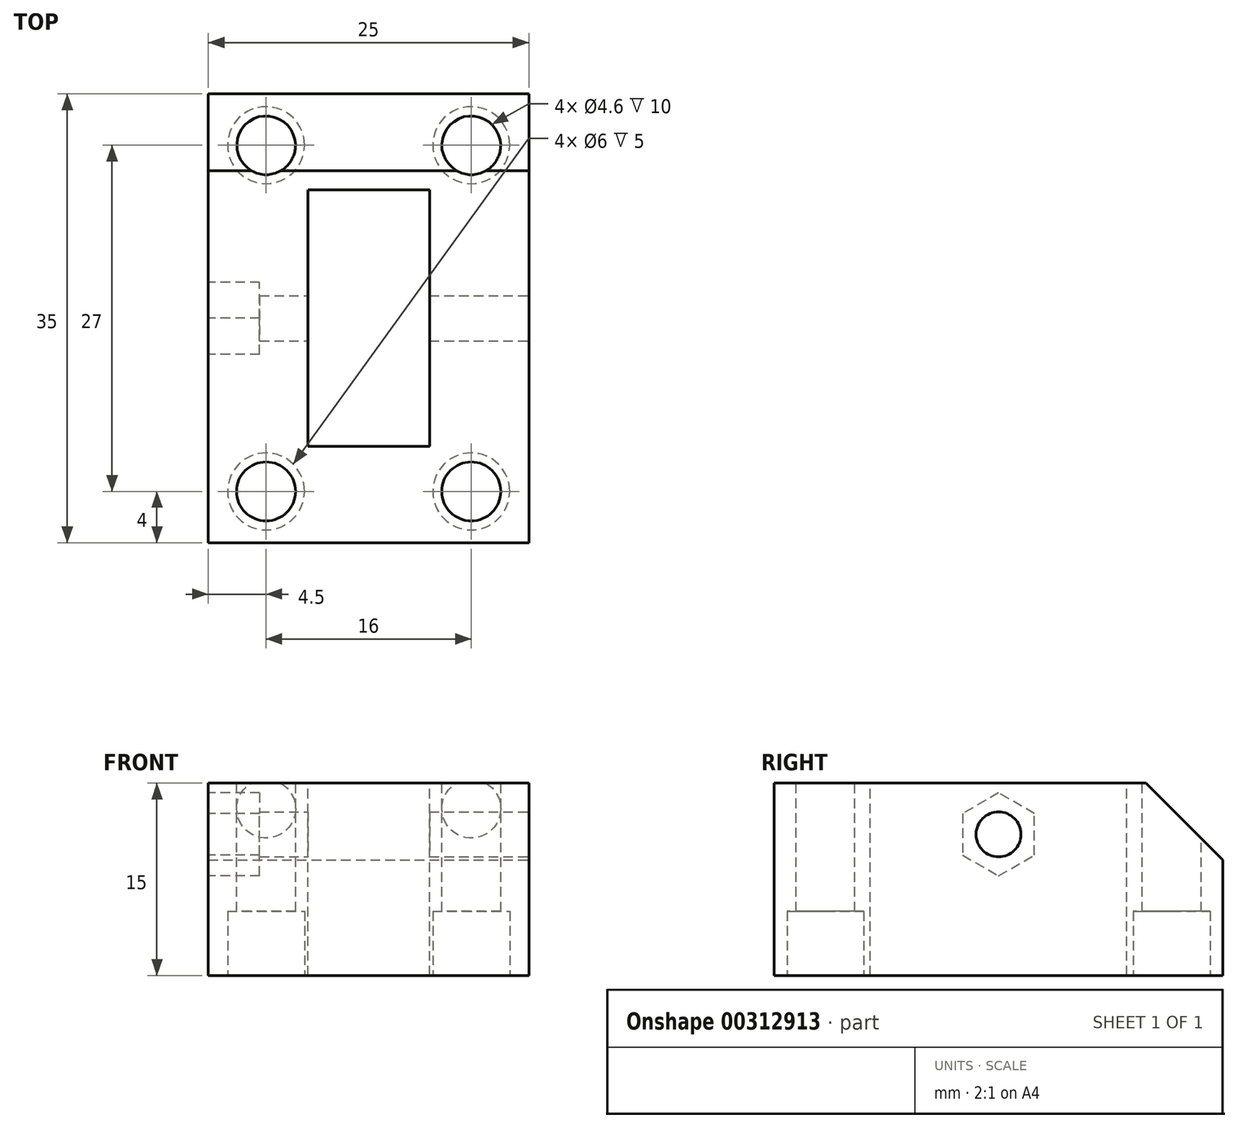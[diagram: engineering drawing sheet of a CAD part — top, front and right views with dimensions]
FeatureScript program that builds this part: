
annotation { "Feature Type Name" : "Feature", "Feature Type Description" : "" }
export const myFeature = defineFeature(function(context is Context, id is Id, definition is map)
    precondition{}
    {
        {
            var Q0;
            Q0=qCreatedBy(makeId("Top.planeOp"),FACE);
            var sketch = newSketch(context, id + "F0", { "sketchPlane" : qUnion([Q0])});
            skLineSegment(sketch, "E0.bottom", {"start": v(-12.5, 17.5) * mm, "end": v(12.5, 17.5) * mm});
            skLineSegment(sketch, "E0.top", {"start": v(-12.5, -17.5) * mm, "end": v(12.5, -17.5) * mm});
            skLineSegment(sketch, "E0.left", {"start": v(-12.5, 17.5) * mm, "end": v(-12.5, -17.5) * mm});
            skLineSegment(sketch, "E0.right", {"start": v(12.5, 17.5) * mm, "end": v(12.5, -17.5) * mm});
            skSolve(sketch);
        }
        {
            var Q0;
            Q0=makeQuery(id+"F0.imprint","IMPRINT",FACE,{"disambiguationData":[TD([[makeQuery(id+"F0.imprint","IMPRINT",EDGE,{"derivedFrom":sQuery(id+"F0.wireOp",EDGE,"E0.bottom")}),-1.0]])]});
            extrude(context, id + "F1", {"entities" : qUnion([Q0]), "oppositeDirection" : true, "depth" : 15 * mm});
        }
        {
            var Q0;
            Q0=makeQuery(id+"F1.opExtrude","SWEPT_FACE",FACE,{"disambiguationData":[OSD([sQuery(id+"F0.wireOp",EDGE,"E0.right")])]});
            var sketch = newSketch(context, id + "F2", { "sketchPlane" : qUnion([Q0])});
            skCircle(sketch, "E1", {"center": v(0, -4) * mm, "radius": 1.75 * mm});
            skSolve(sketch);
        }
        {
            var Q0;
            Q0=makeQuery(id+"F2.imprint","IMPRINT",FACE,{"disambiguationData":[TD([[makeQuery(id+"F2.imprint","IMPRINT",EDGE,{"derivedFrom":sQuery(id+"F2.wireOp",EDGE,"E1")}),1.0]])]});
            extrude(context, id + "F3", {"entities" : qUnion([Q0]), "operationType" : NewBodyOperationType.REMOVE, "oppositeDirection" : true, "depth" : 25 * mm});
        }
        {
            var Q0;
            Q0=makeQuery(id+"F1.opExtrude","CAP_FACE",FACE,{"disambiguationData":[OSD([sQuery(id+"F0.wireOp",EDGE,"E0.bottom"),sQuery(id+"F0.wireOp",EDGE,"E0.top"),sQuery(id+"F0.wireOp",EDGE,"E0.left"),sQuery(id+"F0.wireOp",EDGE,"E0.right")])],"isStart":true});
            var sketch = newSketch(context, id + "F4", { "sketchPlane" : qUnion([Q0])});
            skLineSegment(sketch, "E2.bottom", {"start": v(-4.75, 10) * mm, "end": v(4.75, 10) * mm});
            skLineSegment(sketch, "E2.top", {"start": v(-4.75, -10) * mm, "end": v(4.75, -10) * mm});
            skLineSegment(sketch, "E2.left", {"start": v(-4.75, 10) * mm, "end": v(-4.75, -10) * mm});
            skLineSegment(sketch, "E2.right", {"start": v(4.75, 10) * mm, "end": v(4.75, -10) * mm});
            skSolve(sketch);
        }
        {
            var Q0;
            Q0=makeQuery(id+"F4.imprint","IMPRINT",FACE,{"disambiguationData":[TD([[makeQuery(id+"F4.imprint","IMPRINT",EDGE,{"derivedFrom":sQuery(id+"F4.wireOp",EDGE,"E2.bottom")}),-1.0]])]});
            extrude(context, id + "F5", {"entities" : qUnion([Q0]), "operationType" : NewBodyOperationType.REMOVE, "oppositeDirection" : true, "depth" : 15 * mm});
        }
        {
            var Q0;
            Q0=makeQuery(id+"F1.opExtrude","SWEPT_FACE",FACE,{"disambiguationData":[OSD([sQuery(id+"F0.wireOp",EDGE,"E0.left")])]});
            var sketch = newSketch(context, id + "F6", { "sketchPlane" : qUnion([Q0])});
            skCircle(sketch, "E3.cCircle", {"center": v(0, -4) * mm, "radius": 2.8 * mm, "construction": true});
            skLineSegment(sketch, "E3.0", {"start": v(-2.8, -5.62) * mm, "end": v(-2.8, -2.38) * mm});
            skLineSegment(sketch, "E3.1", {"start": v(-2.8, -2.38) * mm, "end": v(0, -0.77) * mm});
            skLineSegment(sketch, "E3.2", {"start": v(0, -0.77) * mm, "end": v(2.8, -2.38) * mm});
            skLineSegment(sketch, "E3.3", {"start": v(2.8, -2.38) * mm, "end": v(2.8, -5.62) * mm});
            skLineSegment(sketch, "E3.4", {"start": v(2.8, -5.62) * mm, "end": v(0, -7.23) * mm});
            skLineSegment(sketch, "E3.5", {"start": v(0, -7.23) * mm, "end": v(-2.8, -5.62) * mm});
            skPoint(sketch, "E3.0.midPoint", {"position": v(-2.8, -4) * mm});
            skSolve(sketch);
        }
        {
            var Q0;
            Q0=makeQuery(id+"F6.imprint","IMPRINT",FACE,{"disambiguationData":[TD([[makeQuery(id+"F6.imprint","IMPRINT",EDGE,{"derivedFrom":sQuery(id+"F6.wireOp",EDGE,"E3.0")}),-1.0]])]});
            extrude(context, id + "F7", {"entities" : qUnion([Q0]), "operationType" : NewBodyOperationType.REMOVE, "oppositeDirection" : true, "depth" : 4 * mm});
        }
        {
            var Q0;
            Q0=makeQuery(id+"F1.opExtrude","CAP_FACE",FACE,{"disambiguationData":[OSD([sQuery(id+"F0.wireOp",EDGE,"E0.bottom"),sQuery(id+"F0.wireOp",EDGE,"E0.top"),sQuery(id+"F0.wireOp",EDGE,"E0.left"),sQuery(id+"F0.wireOp",EDGE,"E0.right")])],"isStart":true});
            var sketch = newSketch(context, id + "F8", { "sketchPlane" : qUnion([Q0])});
            skCircle(sketch, "E4", {"center": v(-8, 13.5) * mm, "radius": 2.3 * mm});
            skCircle(sketch, "E5", {"center": v(8, 13.5) * mm, "radius": 2.3 * mm});
            skCircle(sketch, "E6", {"center": v(8, -13.5) * mm, "radius": 2.3 * mm});
            skCircle(sketch, "E7", {"center": v(-8, -13.5) * mm, "radius": 2.3 * mm});
            skSolve(sketch);
        }
        {
            var Q0;
            Q0=makeQuery(id+"F8.imprint","IMPRINT",FACE,{"disambiguationData":[TD([[makeQuery(id+"F8.imprint","IMPRINT",EDGE,{"derivedFrom":sQuery(id+"F8.wireOp",EDGE,"E4")}),1.0]])]});
            var Q1;
            Q1=makeQuery(id+"F8.imprint","IMPRINT",FACE,{"disambiguationData":[TD([[makeQuery(id+"F8.imprint","IMPRINT",EDGE,{"derivedFrom":sQuery(id+"F8.wireOp",EDGE,"E5")}),1.0]])]});
            var Q2;
            Q2=makeQuery(id+"F8.imprint","IMPRINT",FACE,{"disambiguationData":[TD([[makeQuery(id+"F8.imprint","IMPRINT",EDGE,{"derivedFrom":sQuery(id+"F8.wireOp",EDGE,"E6")}),1.0]])]});
            var Q3;
            Q3=makeQuery(id+"F8.imprint","IMPRINT",FACE,{"disambiguationData":[TD([[makeQuery(id+"F8.imprint","IMPRINT",EDGE,{"derivedFrom":sQuery(id+"F8.wireOp",EDGE,"E7")}),1.0]])]});
            extrude(context, id + "F9", {"entities" : qUnion([Q0, Q1, Q2, Q3]), "operationType" : NewBodyOperationType.REMOVE, "oppositeDirection" : true, "depth" : 15 * mm});
        }
        {
            var Q0;
            Q0=makeQuery(id+"F1.opExtrude","CAP_FACE",FACE,{"disambiguationData":[OSD([sQuery(id+"F0.wireOp",EDGE,"E0.bottom"),sQuery(id+"F0.wireOp",EDGE,"E0.top"),sQuery(id+"F0.wireOp",EDGE,"E0.left"),sQuery(id+"F0.wireOp",EDGE,"E0.right")])],"isStart":false});
            var sketch = newSketch(context, id + "F10", { "sketchPlane" : qUnion([Q0])});
            skCircle(sketch, "E8", {"center": v(-8, 13.5) * mm, "radius": 3 * mm});
            skCircle(sketch, "E9", {"center": v(8, 13.5) * mm, "radius": 3 * mm});
            skCircle(sketch, "E10", {"center": v(8, -13.5) * mm, "radius": 3 * mm});
            skCircle(sketch, "E11", {"center": v(-8, -13.5) * mm, "radius": 3 * mm});
            skSolve(sketch);
        }
        {
            var Q0;
            Q0=makeQuery(id+"F10.imprint","IMPRINT",FACE,{"disambiguationData":[TD([[makeQuery(id+"F10.imprint","IMPRINT",EDGE,{"derivedFrom":sQuery(id+"F10.wireOp",EDGE,"E8")}),1.0]])]});
            var Q1;
            Q1=makeQuery(id+"F10.imprint","IMPRINT",FACE,{"disambiguationData":[TD([[makeQuery(id+"F10.imprint","IMPRINT",EDGE,{"derivedFrom":sQuery(id+"F10.wireOp",EDGE,"E9")}),1.0]])]});
            var Q2;
            Q2=makeQuery(id+"F10.imprint","IMPRINT",FACE,{"disambiguationData":[TD([[makeQuery(id+"F10.imprint","IMPRINT",EDGE,{"derivedFrom":sQuery(id+"F10.wireOp",EDGE,"E10")}),1.0]])]});
            var Q3;
            Q3=makeQuery(id+"F10.imprint","IMPRINT",FACE,{"disambiguationData":[TD([[makeQuery(id+"F10.imprint","IMPRINT",EDGE,{"derivedFrom":sQuery(id+"F10.wireOp",EDGE,"E11")}),1.0]])]});
            extrude(context, id + "F11", {"entities" : qUnion([Q0, Q1, Q2, Q3]), "operationType" : NewBodyOperationType.REMOVE, "oppositeDirection" : true, "depth" : 5 * mm});
        }
        {
            var Q0;
            Q0=makeQuery(id+"F1.opExtrude","CAP_EDGE",EDGE,{"disambiguationData":[OSD([sQuery(id+"F0.wireOp",EDGE,"E0.bottom")])],"isStart":true});
            chamfer(context, id + "F12", {"entities" : qUnion([Q0]), "width" : 6 * mm, "tangentPropagation" : true});
        }
    });
